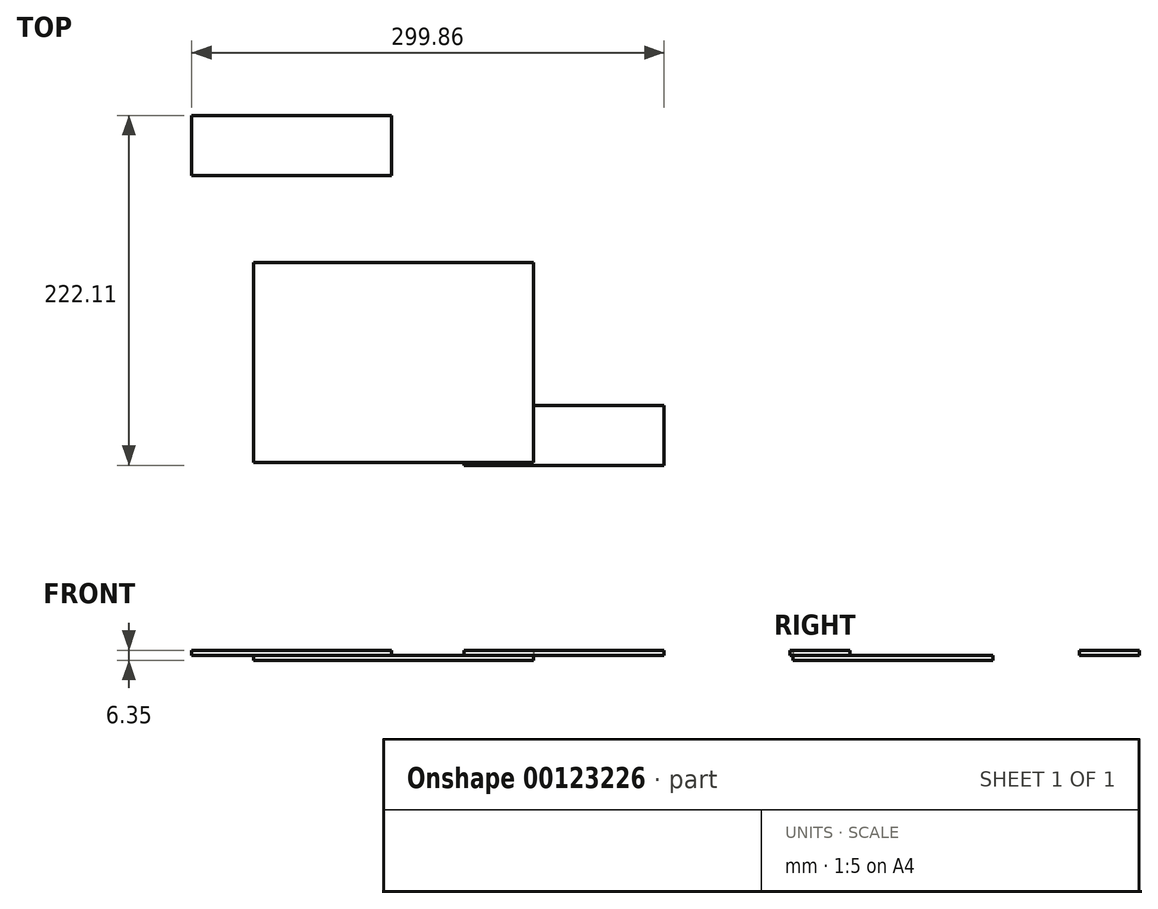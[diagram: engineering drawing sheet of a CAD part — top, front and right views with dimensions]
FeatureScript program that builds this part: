
annotation { "Feature Type Name" : "Feature", "Feature Type Description" : "" }
export const myFeature = defineFeature(function(context is Context, id is Id, definition is map)
    precondition{}
    {
        {
            var Q0;
            Q0=qCreatedBy(makeId("Top.planeOp"),FACE);
            var sketch = newSketch(context, id + "F0", { "sketchPlane" : qUnion([Q0])});
            skLineSegment(sketch, "E0.bottom", {"start": v(-92.56, 25.45) * mm, "end": v(85.24, 25.45) * mm});
            skLineSegment(sketch, "E0.top", {"start": v(-92.56, -101.55) * mm, "end": v(85.24, -101.55) * mm});
            skLineSegment(sketch, "E0.left", {"start": v(-92.56, 25.45) * mm, "end": v(-92.56, -101.55) * mm});
            skLineSegment(sketch, "E0.right", {"start": v(85.24, 25.45) * mm, "end": v(85.24, -101.55) * mm});
            skSolve(sketch);
        }
        {
            var Q0;
            Q0=makeQuery(id+"F0.imprint","IMPRINT",FACE,{"disambiguationData":[TD([[makeQuery(id+"F0.imprint","IMPRINT",EDGE,{"derivedFrom":sQuery(id+"F0.wireOp",EDGE,"E0.bottom")}),-1.0]])]});
            extrude(context, id + "F1", {"entities" : qUnion([Q0]), "depth" : 3.17 * mm});
        }
        {
            var Q0;
            Q0=makeQuery(id+"F1.opExtrude","CAP_FACE",FACE,{"disambiguationData":[OSD([sQuery(id+"F0.wireOp",EDGE,"E0.bottom"),sQuery(id+"F0.wireOp",EDGE,"E0.top"),sQuery(id+"F0.wireOp",EDGE,"E0.left"),sQuery(id+"F0.wireOp",EDGE,"E0.right")])],"isStart":false});
            var sketch = newSketch(context, id + "F2", { "sketchPlane" : qUnion([Q0])});
            skSolve(sketch);
        }
        {
            var Q0;
            Q0=makeQuery(id+"F2.imprint","IMPRINT",FACE,{"disambiguationData":[TD([[makeQuery(id+"F2.imprint","IMPRINT",EDGE,{"derivedFrom":makeQuery(id+"F1.opExtrude","CAP_EDGE",EDGE,{"disambiguationData":[OSD([sQuery(id+"F0.wireOp",EDGE,"E0.bottom")])],"isStart":false})}),-1.0]])]});
            var sketch = newSketch(context, id + "F3", { "sketchPlane" : qUnion([Q0])});
            skLineSegment(sketch, "E1.bottom", {"start": v(40.99, -65.34) * mm, "end": v(167.99, -65.34) * mm});
            skLineSegment(sketch, "E1.top", {"start": v(40.99, -103.44) * mm, "end": v(167.99, -103.44) * mm});
            skLineSegment(sketch, "E1.left", {"start": v(40.99, -65.34) * mm, "end": v(40.99, -103.44) * mm});
            skLineSegment(sketch, "E1.right", {"start": v(167.99, -65.34) * mm, "end": v(167.99, -103.44) * mm});
            skSolve(sketch);
        }
        {
            var Q0;
            {var subQ1=sQuery(id+"F3.wireOp",EDGE,"E1.top");Q0=makeQuery(id+"F3.imprint","IMPRINT",FACE,{"disambiguationData":[TD([[makeQuery(id+"F3.imprint","IMPRINT",EDGE,{"derivedFrom":subQ1}),1.0]])]});}
            extrude(context, id + "F4", {"entities" : qUnion([Q0]), "depth" : 3.17 * mm});
        }
        {
            var Q0;
            Q0=makeQuery(id+"F2.imprint","IMPRINT",FACE,{"disambiguationData":[TD([[makeQuery(id+"F2.imprint","IMPRINT",EDGE,{"derivedFrom":makeQuery(id+"F1.opExtrude","CAP_EDGE",EDGE,{"disambiguationData":[OSD([sQuery(id+"F0.wireOp",EDGE,"E0.bottom")])],"isStart":false})}),-1.0]])]});
            var sketch = newSketch(context, id + "F5", { "sketchPlane" : qUnion([Q0])});
            skLineSegment(sketch, "E2.bottom", {"start": v(-131.87, 118.67) * mm, "end": v(-4.87, 118.67) * mm});
            skLineSegment(sketch, "E2.top", {"start": v(-131.87, 80.57) * mm, "end": v(-4.87, 80.57) * mm});
            skLineSegment(sketch, "E2.left", {"start": v(-131.87, 118.67) * mm, "end": v(-131.87, 80.57) * mm});
            skLineSegment(sketch, "E2.right", {"start": v(-4.87, 118.67) * mm, "end": v(-4.87, 80.57) * mm});
            skSolve(sketch);
        }
        {
            var Q0;
            Q0=makeQuery(id+"F5.imprint","IMPRINT",FACE,{"disambiguationData":[TD([[makeQuery(id+"F5.imprint","IMPRINT",EDGE,{"derivedFrom":sQuery(id+"F5.wireOp",EDGE,"E2.bottom")}),-1.0]])]});
            extrude(context, id + "F6", {"entities" : qUnion([Q0]), "depth" : 3.17 * mm});
        }
    });
